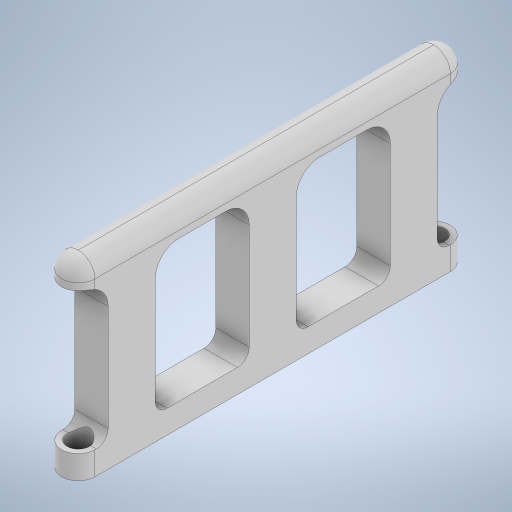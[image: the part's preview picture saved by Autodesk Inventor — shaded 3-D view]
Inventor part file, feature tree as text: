
AUTODESK INVENTOR PART (.ipt)
format: ipt  version: 2023 (Build 270158000, 158)  size: 363,008 bytes
history: native  units: in
note: dims shown in document units (in); Inventor stores cm internally (conversion verified against a paired STEP export)
features: sketch x9, extrude x8, fillet x3
ambient origin geometry x8: Origin, YZ Plane, XZ Plane, XY Plane, X Axis, Y Axis, Z Axis, Center Point
bodies: Solid1 (feature_tree)
feature tree (20):
  extrude  "Extrusion1"  Depth=0.1161in
  extrude  "Extrusion2"  Depth=3.78in
  extrude  "Extrusion3"  Depth=0.25in TaperAngle=0.0deg
  extrude  "Extrusion4"  Depth=0.25in TaperAngle=0.0deg
  extrude  "Extrusion5"  Depth=0.2in TaperAngle=0.0deg
  extrude  "Extrusion6"  Depth=0.25in TaperAngle=0.0deg
  sketch  "Sketch7"  dims[d19=0.2362in d20=0.2in d21=0.0in d23=0.5in]
  extrude  "Extrusion7"  Depth=0.5in TaperAngle=0.0deg
  fillet  "Fillet1"  Radius=0.5in
  extrude  "Extrusion8"  Depth=0.5in
  fillet  "Fillet2"  Radius=1.5in
  fillet  "Fillet3"  Radius=0.125in
  sketch  "Sketch1"  dims[d0=0.3543in d1=0.1161in]
  sketch  "Sketch2"  dims[d2=0.2362in d3=3.78in]
  sketch  "Sketch3"  dims[d5=0.3543in d6=0.1161in d7=0.2362in d8=0.25in d9=0.0in]
  sketch  "Sketch4"  dims[d10=0.1161in d11=0.25in d12=0.0in]
  sketch  "Sketch5"  dims[d13=0.2362in d14=0.2in d15=0.0in]
  sketch  "Sketch6"  dims[d16=0.1161in d17=0.25in d18=0.0in]
  sketch  "Sketch8"  dims[d24=1.5in d25=0.0in d29=0.5in d30=1.5in d31=0.0in d32=0.125in]
  sketch  "Sketch9"  dims[d33=0.25in d34=0.0in d35=0.1772in d36=0.25in d37=0.0in d38=0.0in d39=0.0in d40=0.0in]
